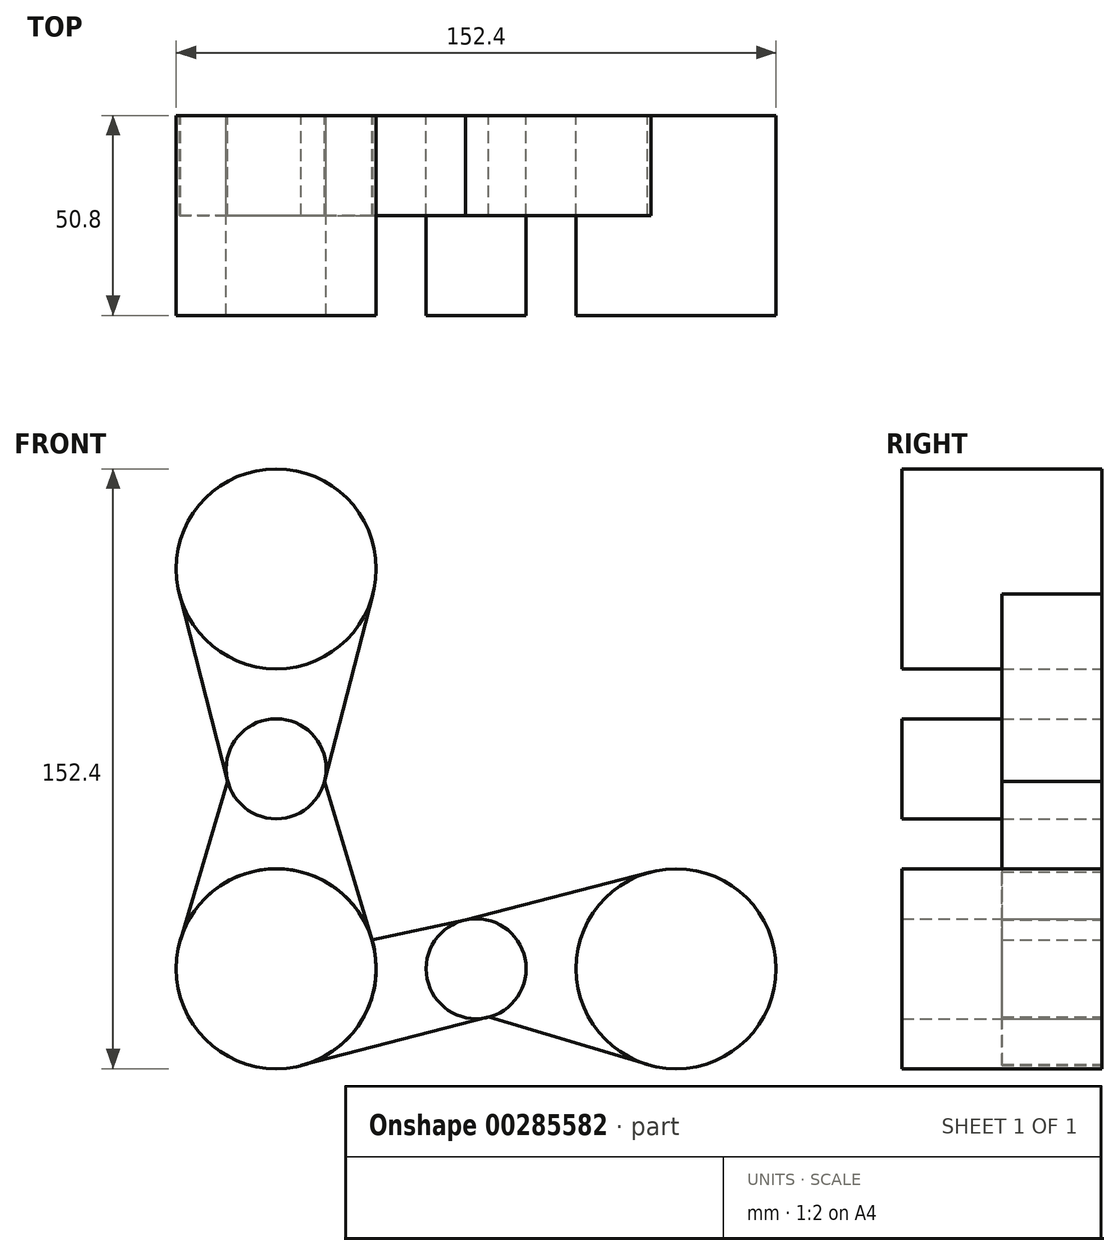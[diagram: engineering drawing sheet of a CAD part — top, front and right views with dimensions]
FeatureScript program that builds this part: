
annotation { "Feature Type Name" : "Feature", "Feature Type Description" : "" }
export const myFeature = defineFeature(function(context is Context, id is Id, definition is map)
    precondition{}
    {
        {
            var Q0;
            Q0=qCreatedBy(makeId("Front.planeOp"),FACE);
            var sketch = newSketch(context, id + "F0", { "sketchPlane" : qUnion([Q0])});
            skLineSegment(sketch, "E0", {"start": v(-137.59, -77.75) * mm, "end": v(-86.79, -77.75) * mm});
            skLineSegment(sketch, "E1", {"start": v(-86.79, -77.75) * mm, "end": v(-35.99, -77.75) * mm});
            skLineSegment(sketch, "E2", {"start": v(-137.59, -77.75) * mm, "end": v(-137.59, -26.95) * mm});
            skLineSegment(sketch, "E3", {"start": v(-137.59, -26.95) * mm, "end": v(-137.59, 23.85) * mm});
            skCircle(sketch, "E4", {"center": v(-137.59, 23.85) * mm, "radius": 25.4 * mm});
            skCircle(sketch, "E5", {"center": v(-35.99, -77.75) * mm, "radius": 25.4 * mm});
            skCircle(sketch, "E6", {"center": v(-137.59, -77.75) * mm, "radius": 25.4 * mm});
            skCircle(sketch, "E7", {"center": v(-86.79, -77.75) * mm, "radius": 12.7 * mm});
            skCircle(sketch, "E8", {"center": v(-137.59, -26.95) * mm, "radius": 12.7 * mm});
            skLineSegment(sketch, "E9", {"start": v(-162.18, 17.5) * mm, "end": v(-149.88, -30.13) * mm});
            skLineSegment(sketch, "E10", {"start": v(-149.88, -30.13) * mm, "end": v(-161.93, -70.5) * mm});
            skLineSegment(sketch, "E11", {"start": v(-113, 17.5) * mm, "end": v(-125.3, -30.13) * mm});
            skLineSegment(sketch, "E12", {"start": v(-125.3, -30.13) * mm, "end": v(-113.25, -70.5) * mm});
            skLineSegment(sketch, "E13", {"start": v(-113.25, -70.5) * mm, "end": v(-89.48, -65.34) * mm});
            skLineSegment(sketch, "E14", {"start": v(-89.48, -65.34) * mm, "end": v(-42.34, -53.16) * mm});
            skLineSegment(sketch, "E15", {"start": v(-131.24, -102.35) * mm, "end": v(-83.61, -90.05) * mm});
            skLineSegment(sketch, "E16", {"start": v(-83.61, -90.05) * mm, "end": v(-43.25, -102.1) * mm});
            skSolve(sketch);
        }
        {
            var Q0;
            {var subQ0=sQuery(id+"F0.wireOp",EDGE,"E4");var subQ1=makeQuery(id+"F0.imprint","INTERSECT",VERTEX,{"derivedFrom":[subQ0,sQuery(id+"F0.wireOp",EDGE,"E9")]});Q0=makeQuery(id+"F0.imprint","IMPRINT",FACE,{"disambiguationData":[TD([[makeQuery(id+"F0.imprint","IMPRINT",EDGE,{"disambiguationData":[TD([[subQ1,-1.0]])],"derivedFrom":subQ0}),1.0]])]});}
            var Q1;
            {var subQ0=sQuery(id+"F0.wireOp",EDGE,"E3");var subQ1=sQuery(id+"F0.wireOp",EDGE,"E2");var subQ2=makeQuery(id+"F0.imprint","INTERSECT",VERTEX,{"derivedFrom":[subQ1,subQ0]});Q1=makeQuery(id+"F0.imprint","IMPRINT",FACE,{"disambiguationData":[TD([[makeQuery(id+"F0.imprint","IMPRINT",EDGE,{"disambiguationData":[TD([[subQ2,1.0]])],"derivedFrom":subQ1}),1.0]])]});}
            var Q2;
            {var subQ0=sQuery(id+"F0.wireOp",EDGE,"E2");var subQ1=sQuery(id+"F0.wireOp",EDGE,"E0");var subQ2=makeQuery(id+"F0.imprint","INTERSECT",VERTEX,{"derivedFrom":[subQ1,subQ0]});Q2=makeQuery(id+"F0.imprint","IMPRINT",FACE,{"disambiguationData":[TD([[makeQuery(id+"F0.imprint","IMPRINT",EDGE,{"disambiguationData":[TD([[subQ2,-1.0]])],"derivedFrom":subQ1}),1.0]])]});}
            var Q3;
            {var subQ3=sQuery(id+"F0.wireOp",EDGE,"E2");var subQ5=sQuery(id+"F0.wireOp",EDGE,"E0");var subQ6=makeQuery(id+"F0.imprint","INTERSECT",VERTEX,{"derivedFrom":[subQ5,subQ3]});Q3=makeQuery(id+"F0.imprint","IMPRINT",FACE,{"disambiguationData":[TD([[makeQuery(id+"F0.imprint","IMPRINT",EDGE,{"disambiguationData":[TD([[subQ6,-1.0]])],"derivedFrom":subQ5}),-1.0]])]});}
            var Q4;
            {var subQ0=sQuery(id+"F0.wireOp",EDGE,"E3");var subQ1=sQuery(id+"F0.wireOp",EDGE,"E2");var subQ2=makeQuery(id+"F0.imprint","INTERSECT",VERTEX,{"derivedFrom":[subQ1,subQ0]});Q4=makeQuery(id+"F0.imprint","IMPRINT",FACE,{"disambiguationData":[TD([[makeQuery(id+"F0.imprint","IMPRINT",EDGE,{"disambiguationData":[TD([[subQ2,1.0]])],"derivedFrom":subQ1}),-1.0]])]});}
            var Q5;
            {var subQ0=sQuery(id+"F0.wireOp",EDGE,"E1");var subQ1=sQuery(id+"F0.wireOp",EDGE,"E0");var subQ2=makeQuery(id+"F0.imprint","INTERSECT",VERTEX,{"derivedFrom":[subQ1,subQ0]});Q5=makeQuery(id+"F0.imprint","IMPRINT",FACE,{"disambiguationData":[TD([[makeQuery(id+"F0.imprint","IMPRINT",EDGE,{"disambiguationData":[TD([[subQ2,1.0]])],"derivedFrom":subQ1}),1.0]])]});}
            var Q6;
            {var subQ0=sQuery(id+"F0.wireOp",EDGE,"E1");var subQ1=sQuery(id+"F0.wireOp",EDGE,"E0");var subQ2=makeQuery(id+"F0.imprint","INTERSECT",VERTEX,{"derivedFrom":[subQ1,subQ0]});Q6=makeQuery(id+"F0.imprint","IMPRINT",FACE,{"disambiguationData":[TD([[makeQuery(id+"F0.imprint","IMPRINT",EDGE,{"disambiguationData":[TD([[subQ2,1.0]])],"derivedFrom":subQ1}),-1.0]])]});}
            var Q7;
            {var subQ0=sQuery(id+"F0.wireOp",EDGE,"E5");var subQ1=makeQuery(id+"F0.imprint","INTERSECT",VERTEX,{"derivedFrom":[subQ0,sQuery(id+"F0.wireOp",EDGE,"E14")]});Q7=makeQuery(id+"F0.imprint","IMPRINT",FACE,{"disambiguationData":[TD([[makeQuery(id+"F0.imprint","IMPRINT",EDGE,{"disambiguationData":[TD([[subQ1,-1.0]])],"derivedFrom":subQ0}),1.0]])]});}
            extrude(context, id + "F1", {"entities" : qUnion([Q0, Q1, Q2, Q3, Q4, Q5, Q6, Q7]), "depth" : 50.8 * mm});
        }
        {
            var Q0;
            {var subQ5=sQuery(id+"F0.wireOp",EDGE,"E9");Q0=makeQuery(id+"F0.imprint","IMPRINT",FACE,{"disambiguationData":[TD([[makeQuery(id+"F0.imprint","IMPRINT",EDGE,{"derivedFrom":subQ5}),1.0]])]});}
            var Q1;
            {var subQ5=sQuery(id+"F0.wireOp",EDGE,"E11");Q1=makeQuery(id+"F0.imprint","IMPRINT",FACE,{"disambiguationData":[TD([[makeQuery(id+"F0.imprint","IMPRINT",EDGE,{"derivedFrom":subQ5}),-1.0]])]});}
            var Q2;
            {var subQ5=sQuery(id+"F0.wireOp",EDGE,"E10");Q2=makeQuery(id+"F0.imprint","IMPRINT",FACE,{"disambiguationData":[TD([[makeQuery(id+"F0.imprint","IMPRINT",EDGE,{"derivedFrom":subQ5}),1.0]])]});}
            var Q3;
            {var subQ5=sQuery(id+"F0.wireOp",EDGE,"E12");Q3=makeQuery(id+"F0.imprint","IMPRINT",FACE,{"disambiguationData":[TD([[makeQuery(id+"F0.imprint","IMPRINT",EDGE,{"derivedFrom":subQ5}),-1.0]])]});}
            var Q4;
            {var subQ5=sQuery(id+"F0.wireOp",EDGE,"E15");Q4=makeQuery(id+"F0.imprint","IMPRINT",FACE,{"disambiguationData":[TD([[makeQuery(id+"F0.imprint","IMPRINT",EDGE,{"derivedFrom":subQ5}),1.0]])]});}
            var Q5;
            {var subQ5=sQuery(id+"F0.wireOp",EDGE,"E13");Q5=makeQuery(id+"F0.imprint","IMPRINT",FACE,{"disambiguationData":[TD([[makeQuery(id+"F0.imprint","IMPRINT",EDGE,{"derivedFrom":subQ5}),-1.0]])]});}
            var Q6;
            {var subQ5=sQuery(id+"F0.wireOp",EDGE,"E16");Q6=makeQuery(id+"F0.imprint","IMPRINT",FACE,{"disambiguationData":[TD([[makeQuery(id+"F0.imprint","IMPRINT",EDGE,{"derivedFrom":subQ5}),1.0]])]});}
            var Q7;
            {var subQ5=sQuery(id+"F0.wireOp",EDGE,"E14");Q7=makeQuery(id+"F0.imprint","IMPRINT",FACE,{"disambiguationData":[TD([[makeQuery(id+"F0.imprint","IMPRINT",EDGE,{"derivedFrom":subQ5}),-1.0]])]});}
            extrude(context, id + "F2", {"entities" : qUnion([Q0, Q1, Q2, Q3, Q4, Q5, Q6, Q7]), "depth" : 25.4 * mm});
        }
    });
